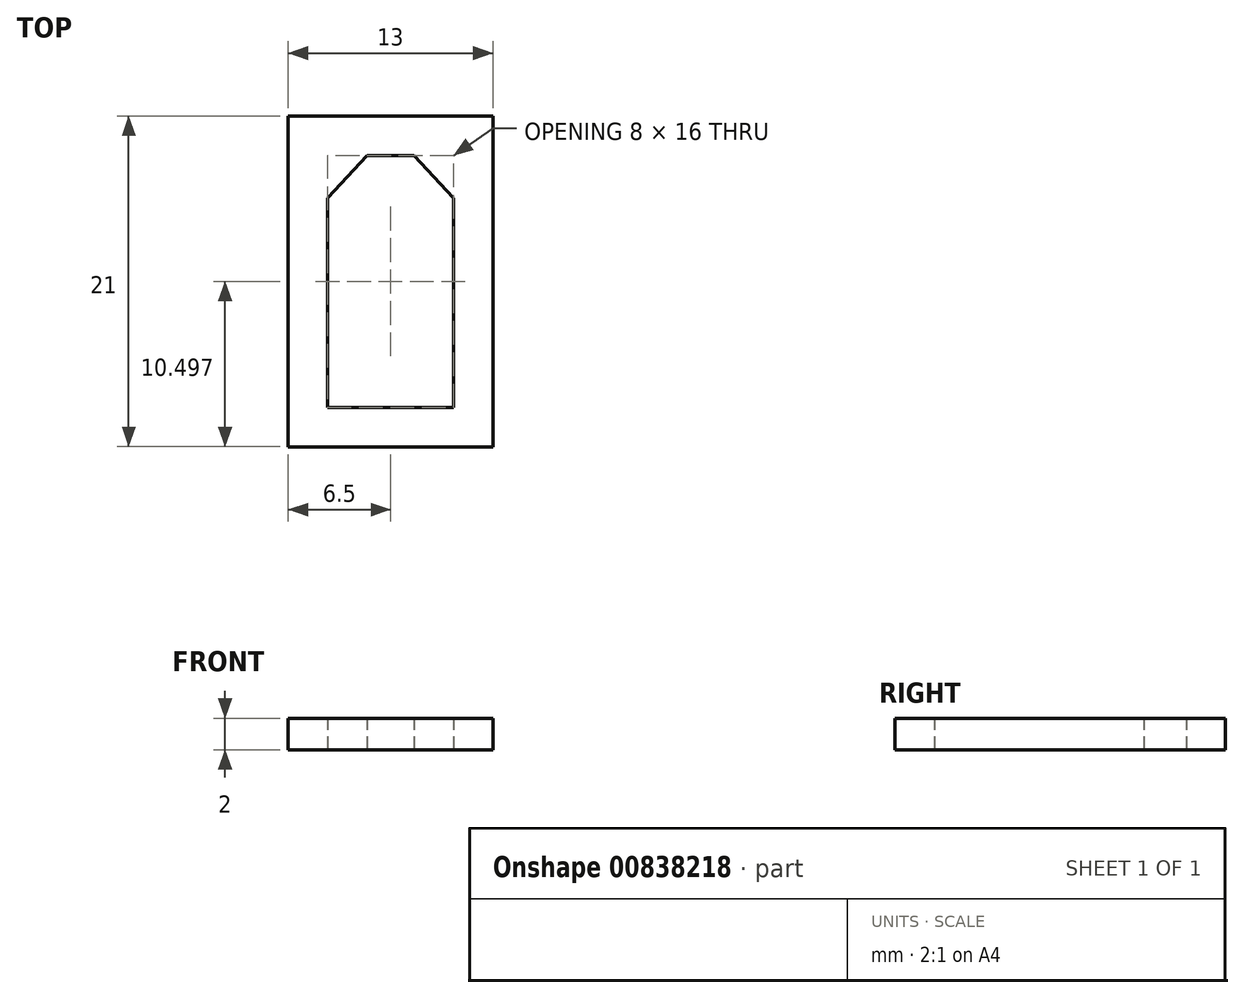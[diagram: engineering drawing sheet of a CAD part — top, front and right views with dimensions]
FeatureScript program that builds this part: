
annotation { "Feature Type Name" : "Feature", "Feature Type Description" : "" }
export const myFeature = defineFeature(function(context is Context, id is Id, definition is map)
    precondition{}
    {
        {
            var Q0;
            Q0=qCreatedBy(makeId("Top.planeOp"),FACE);
            var sketch = newSketch(context, id + "F0", { "sketchPlane" : qUnion([Q0])});
            skLineSegment(sketch, "E0", {"start": v(0, 26.86) * mm, "end": v(0, -31.4) * mm, "construction": true});
            skLineSegment(sketch, "E1", {"start": v(0, -5.1) * mm, "end": v(-4, -5.1) * mm});
            skLineSegment(sketch, "E2", {"start": v(-4, -5.1) * mm, "end": v(-4, 8.2) * mm});
            skLineSegment(sketch, "E3", {"start": v(-4, 8.2) * mm, "end": v(-1.5, 10.9) * mm});
            skLineSegment(sketch, "E4", {"start": v(-1.5, 10.9) * mm, "end": v(0, 10.9) * mm});
            skLineSegment(sketch, "E5.MirrorCS", {"start": v(4, -5.1) * mm, "end": v(4, 8.2) * mm});
            skLineSegment(sketch, "E6.MirrorCS", {"start": v(4, 8.2) * mm, "end": v(1.5, 10.9) * mm});
            skLineSegment(sketch, "E7.MirrorCS", {"start": v(1.5, 10.9) * mm, "end": v(0, 10.9) * mm});
            skLineSegment(sketch, "E8.MirrorCS", {"start": v(0, -5.1) * mm, "end": v(4, -5.1) * mm});
            skLineSegment(sketch, "E9.bottom", {"start": v(-6.5, -7.6) * mm, "end": v(6.5, -7.6) * mm});
            skLineSegment(sketch, "E9.top", {"start": v(-6.5, 13.4) * mm, "end": v(6.5, 13.4) * mm});
            skLineSegment(sketch, "E9.left", {"start": v(-6.5, -7.6) * mm, "end": v(-6.5, 13.4) * mm});
            skLineSegment(sketch, "E9.right", {"start": v(6.5, -7.6) * mm, "end": v(6.5, 13.4) * mm});
            skSolve(sketch);
        }
        {
            var Q0;
            Q0 = qSketchRegion(id + "F0", true);
            extrude(context, id + "F1", {"entities" : qUnion([Q0]), "depth" : 2 * mm, "offsetDistance" : 25 * mm});
        }
    });
